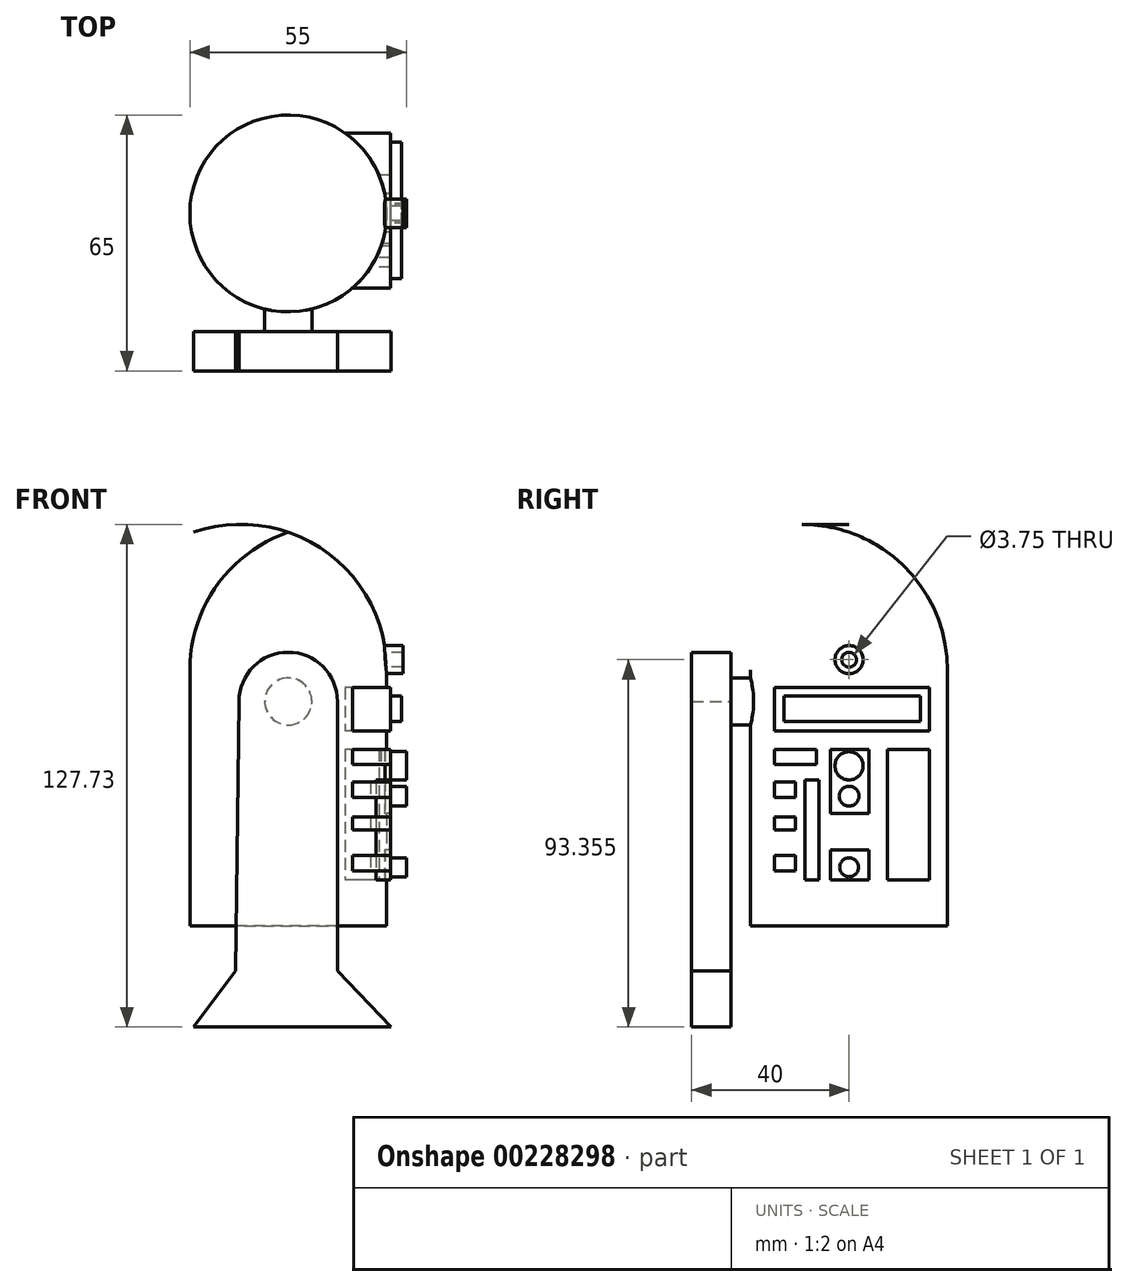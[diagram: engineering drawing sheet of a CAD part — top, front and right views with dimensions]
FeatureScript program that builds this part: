
annotation { "Feature Type Name" : "Feature", "Feature Type Description" : "" }
export const myFeature = defineFeature(function(context is Context, id is Id, definition is map)
    precondition{}
    {
        {
            var Q0;
            Q0=qCreatedBy(makeId("Front.planeOp"),FACE);
            var sketch = newSketch(context, id + "F0", { "sketchPlane" : qUnion([Q0])});
            skLineSegment(sketch, "E0", {"start": v(0, 0) * mm, "end": v(0, 100) * mm});
            skLineSegment(sketch, "E1", {"start": v(0, 0) * mm, "end": v(25, 0) * mm});
            skLineSegment(sketch, "E2", {"start": v(25, 65) * mm, "end": v(25, 0) * mm});
            skArc(sketch, "E3", {"start": v(25, 65) * mm, "mid": v(18.1, 86.5) * mm, "end": v(0, 100) * mm});
            skSolve(sketch);
        }
        {
            var Q0;
            Q0 = qSketchRegion(id + "F0", true);
            var Q1;
            Q1=sQuery(id+"F0.wireOp",EDGE,"E0");
            revolve(context, id + "F1", {"entities" : qUnion([Q0]), "axis" : qUnion([Q1]), "revolveType" : RevolveType.FULL});
        }
        {
            var Q0;
            Q0=qCreatedBy(makeId("Front.planeOp"),FACE);
            var sketch = newSketch(context, id + "F2", { "sketchPlane" : qUnion([Q0])});
            skCircle(sketch, "E4", {"center": v(0, 57) * mm, "radius": 6 * mm});
            skSolve(sketch);
        }
        {
            var Q0;
            Q0 = qSketchRegion(id + "F2", true);
            extrude(context, id + "F3", {"entities" : qUnion([Q0]), "operationType" : NewBodyOperationType.ADD, "depth" : 30 * mm});
        }
        {
            var Q0;
            Q0=makeQuery(id+"F3.opExtrude","CAP_FACE",FACE,{"disambiguationData":[OSD([sQuery(id+"F2.wireOp",EDGE,"E4")])],"isStart":false});
            var sketch = newSketch(context, id + "F4", { "sketchPlane" : qUnion([Q0])});
            skArc(sketch, "E5", {"start": v(12.5, 57) * mm, "mid": v(0, 69.5) * mm, "end": v(-12.5, 57) * mm});
            skLineSegment(sketch, "E6", {"start": v(12.5, 57) * mm, "end": v(12.5, -11.5) * mm});
            skLineSegment(sketch, "E7", {"start": v(12.5, -11.5) * mm, "end": v(26.08, -25.73) * mm});
            skLineSegment(sketch, "E8", {"start": v(26.08, -25.73) * mm, "end": v(-24, -25.73) * mm});
            skLineSegment(sketch, "E9", {"start": v(-24, -25.73) * mm, "end": v(-13.4, -11.5) * mm});
            skLineSegment(sketch, "E10", {"start": v(-13.4, -11.5) * mm, "end": v(-12.5, 57) * mm});
            skSolve(sketch);
        }
        {
            var Q0;
            Q0 = qSketchRegion(id + "F4", true);
            extrude(context, id + "F5", {"entities" : qUnion([Q0]), "operationType" : NewBodyOperationType.ADD, "depth" : 10 * mm});
        }
        {
            var Q0;
            Q0=qCreatedBy(makeId("Right.planeOp"),FACE);
            var sketch = newSketch(context, id + "F6", { "sketchPlane" : qUnion([Q0])});
            skCircle(sketch, "E11", {"center": v(-12.15, 72.96) * mm, "radius": 3.85 * mm});
            skCircle(sketch, "E12", {"center": v(0, 67.63) * mm, "radius": 3.57 * mm});
            skCircle(sketch, "E13", {"center": v(0, 67.63) * mm, "radius": 1.87 * mm});
            skSolve(sketch);
        }
        {
            var Q0;
            Q0 = qSketchRegion(id + "F6", true);
            extrude(context, id + "F7", {"entities" : qUnion([Q0]), "operationType" : NewBodyOperationType.ADD, "depth" : 29.2 * mm});
        }
        {
            var Q0;
            Q0=qCreatedBy(makeId("Right.planeOp"),FACE);
            var sketch = newSketch(context, id + "F8", { "sketchPlane" : qUnion([Q0])});
            skLineSegment(sketch, "E14.bottom", {"start": v(-4.74, 44.8) * mm, "end": v(5.04, 44.8) * mm});
            skLineSegment(sketch, "E14.top", {"start": v(-4.74, 28.5) * mm, "end": v(5.04, 28.5) * mm});
            skLineSegment(sketch, "E14.left", {"start": v(-4.74, 44.8) * mm, "end": v(-4.74, 28.5) * mm});
            skLineSegment(sketch, "E14.right", {"start": v(5.04, 44.8) * mm, "end": v(5.04, 28.5) * mm});
            skLineSegment(sketch, "E15.bottom", {"start": v(-4.74, 19.32) * mm, "end": v(5.04, 19.32) * mm});
            skLineSegment(sketch, "E15.top", {"start": v(-4.74, 11.61) * mm, "end": v(5.04, 11.61) * mm});
            skLineSegment(sketch, "E15.left", {"start": v(-4.74, 19.32) * mm, "end": v(-4.74, 11.61) * mm});
            skLineSegment(sketch, "E15.right", {"start": v(5.04, 19.32) * mm, "end": v(5.04, 11.61) * mm});
            skLineSegment(sketch, "E16.bottom", {"start": v(9.78, 44.8) * mm, "end": v(20.45, 44.8) * mm});
            skLineSegment(sketch, "E16.top", {"start": v(9.78, 11.61) * mm, "end": v(20.45, 11.61) * mm});
            skLineSegment(sketch, "E16.left", {"start": v(9.78, 44.8) * mm, "end": v(9.78, 11.61) * mm});
            skLineSegment(sketch, "E16.right", {"start": v(20.45, 44.8) * mm, "end": v(20.45, 11.61) * mm});
            skLineSegment(sketch, "E17.bottom", {"start": v(-18.97, 60.51) * mm, "end": v(20.45, 60.51) * mm});
            skLineSegment(sketch, "E17.top", {"start": v(-18.97, 49.55) * mm, "end": v(20.45, 49.55) * mm});
            skLineSegment(sketch, "E17.left", {"start": v(-18.97, 60.51) * mm, "end": v(-18.97, 49.55) * mm});
            skLineSegment(sketch, "E17.right", {"start": v(20.45, 60.51) * mm, "end": v(20.45, 49.55) * mm});
            skLineSegment(sketch, "E18.bottom", {"start": v(-18.97, 44.8) * mm, "end": v(-8.3, 44.8) * mm});
            skLineSegment(sketch, "E18.top", {"start": v(-18.97, 40.95) * mm, "end": v(-8.3, 40.95) * mm});
            skLineSegment(sketch, "E18.left", {"start": v(-18.97, 44.8) * mm, "end": v(-18.97, 40.95) * mm});
            skLineSegment(sketch, "E18.right", {"start": v(-8.3, 44.8) * mm, "end": v(-8.3, 40.95) * mm});
            skLineSegment(sketch, "E19.bottom", {"start": v(-11.26, 37.1) * mm, "end": v(-7.7, 37.1) * mm});
            skLineSegment(sketch, "E19.top", {"start": v(-11.26, 11.61) * mm, "end": v(-7.7, 11.61) * mm});
            skLineSegment(sketch, "E19.left", {"start": v(-11.26, 37.1) * mm, "end": v(-11.26, 11.61) * mm});
            skLineSegment(sketch, "E19.right", {"start": v(-7.7, 37.1) * mm, "end": v(-7.7, 11.61) * mm});
            skLineSegment(sketch, "E20.bottom", {"start": v(-18.97, 36.5) * mm, "end": v(-13.63, 36.5) * mm});
            skLineSegment(sketch, "E20.top", {"start": v(-18.97, 32.65) * mm, "end": v(-13.63, 32.65) * mm});
            skLineSegment(sketch, "E20.left", {"start": v(-18.97, 36.5) * mm, "end": v(-18.97, 32.65) * mm});
            skLineSegment(sketch, "E20.right", {"start": v(-13.63, 36.5) * mm, "end": v(-13.63, 32.65) * mm});
            skPoint(sketch, "E21.oppositeSnap0", {"position": v(-11.26, 24.35) * mm});
            skLineSegment(sketch, "E21.bottom", {"start": v(-18.97, 27.61) * mm, "end": v(-13.63, 27.61) * mm});
            skLineSegment(sketch, "E21.top", {"start": v(-18.97, 24.35) * mm, "end": v(-13.63, 24.35) * mm});
            skLineSegment(sketch, "E21.left", {"start": v(-18.97, 27.61) * mm, "end": v(-18.97, 24.35) * mm});
            skLineSegment(sketch, "E21.right", {"start": v(-13.63, 27.61) * mm, "end": v(-13.63, 24.35) * mm});
            skLineSegment(sketch, "E22.bottom", {"start": v(-18.97, 17.83) * mm, "end": v(-13.63, 17.83) * mm});
            skLineSegment(sketch, "E22.top", {"start": v(-18.97, 13.98) * mm, "end": v(-13.63, 13.98) * mm});
            skLineSegment(sketch, "E22.left", {"start": v(-18.97, 17.83) * mm, "end": v(-18.97, 13.98) * mm});
            skLineSegment(sketch, "E22.right", {"start": v(-13.63, 17.83) * mm, "end": v(-13.63, 13.98) * mm});
            skSolve(sketch);
        }
        {
            var Q0;
            Q0 = qSketchRegion(id + "F8", true);
            extrude(context, id + "F9", {"entities" : qUnion([Q0]), "operationType" : NewBodyOperationType.ADD, "depth" : 26 * mm});
        }
        {
            var Q0;
            Q0=qCreatedBy(makeId("Right.planeOp"),FACE);
            var sketch = newSketch(context, id + "F10", { "sketchPlane" : qUnion([Q0])});
            skCircle(sketch, "E23", {"center": v(0, 40.66) * mm, "radius": 3.58 * mm});
            skCircle(sketch, "E24", {"center": v(0, 32.95) * mm, "radius": 2.51 * mm});
            skCircle(sketch, "E25", {"center": v(0, 14.87) * mm, "radius": 2.39 * mm});
            skSolve(sketch);
        }
        {
            var Q0;
            Q0 = qSketchRegion(id + "F10", true);
            extrude(context, id + "F11", {"entities" : qUnion([Q0]), "operationType" : NewBodyOperationType.ADD, "depth" : 30 * mm});
        }
        {
            var Q0;
            Q0=qCreatedBy(makeId("Right.planeOp"),FACE);
            var sketch = newSketch(context, id + "F12", { "sketchPlane" : qUnion([Q0])});
            skLineSegment(sketch, "E26.bottom", {"start": v(-16.6, 58.44) * mm, "end": v(18.08, 58.44) * mm});
            skLineSegment(sketch, "E26.top", {"start": v(-16.6, 51.92) * mm, "end": v(18.08, 51.92) * mm});
            skLineSegment(sketch, "E26.left", {"start": v(-16.6, 58.44) * mm, "end": v(-16.6, 51.92) * mm});
            skLineSegment(sketch, "E26.right", {"start": v(18.08, 58.44) * mm, "end": v(18.08, 51.92) * mm});
            skSolve(sketch);
        }
        {
            var Q0;
            Q0 = qSketchRegion(id + "F12", true);
            extrude(context, id + "F13", {"entities" : qUnion([Q0]), "operationType" : NewBodyOperationType.ADD, "depth" : 28.8 * mm});
        }
    });
